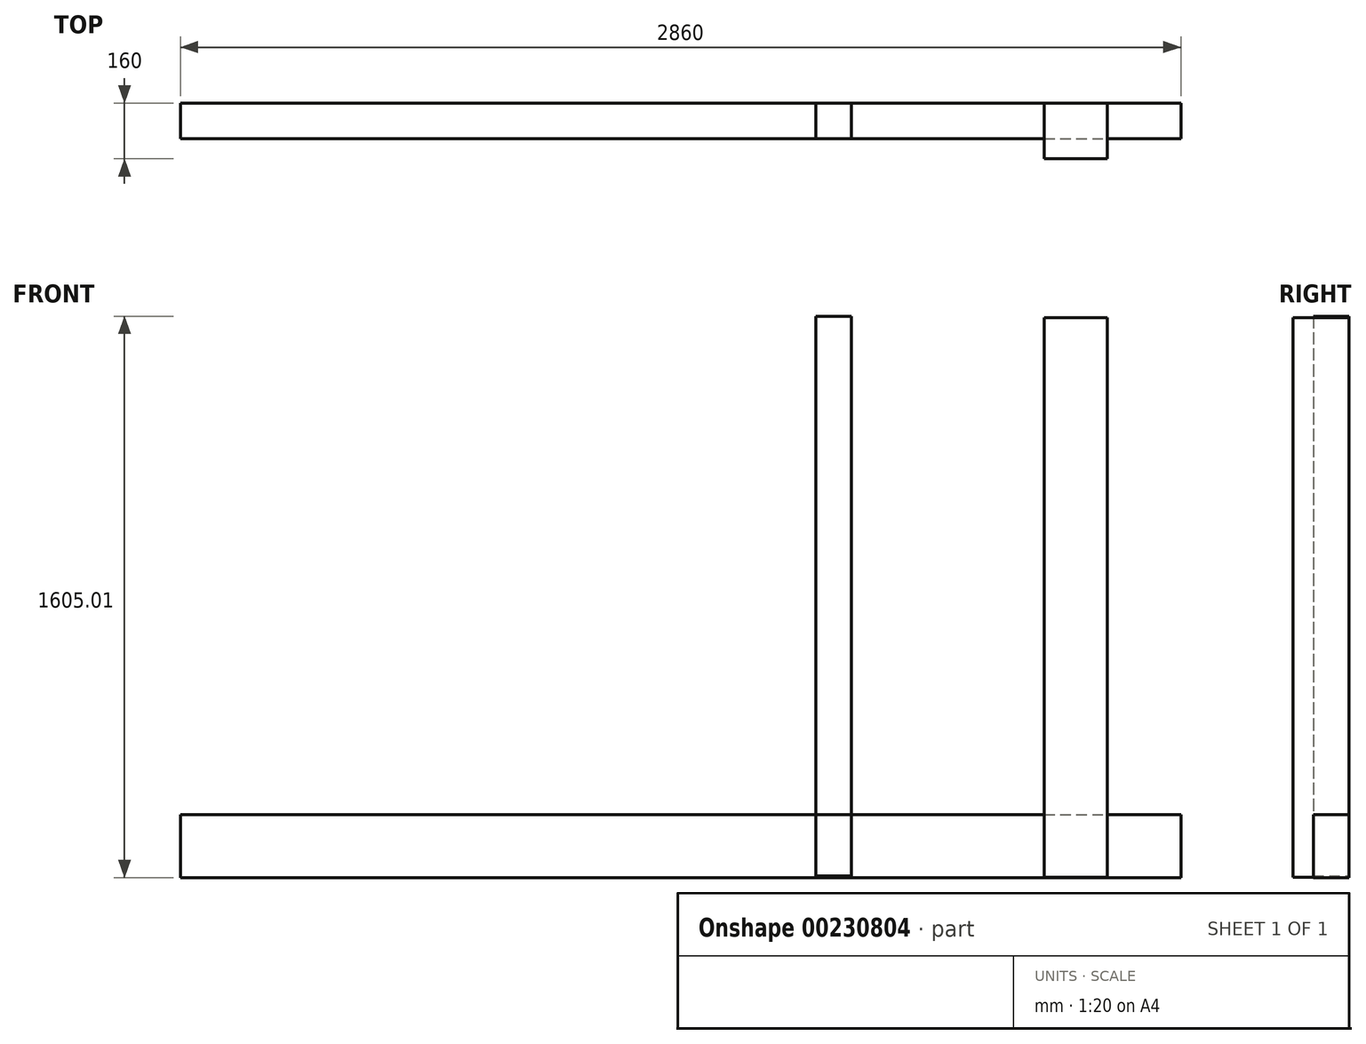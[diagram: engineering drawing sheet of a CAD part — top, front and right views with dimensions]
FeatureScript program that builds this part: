
annotation { "Feature Type Name" : "Feature", "Feature Type Description" : "" }
export const myFeature = defineFeature(function(context is Context, id is Id, definition is map)
    precondition{}
    {
        {
            var Q0;
            Q0=qCreatedBy(makeId("Front.planeOp"),FACE);
            var sketch = newSketch(context, id + "F0", { "sketchPlane" : qUnion([Q0])});
            skLineSegment(sketch, "E0.bottom", {"start": v(-353.4, 789.19) * mm, "end": v(-251.8, 789.19) * mm});
            skLineSegment(sketch, "E0.top", {"start": v(-353.4, -810.81) * mm, "end": v(-251.8, -810.81) * mm});
            skLineSegment(sketch, "E0.left", {"start": v(-353.4, 789.19) * mm, "end": v(-353.4, -810.81) * mm});
            skLineSegment(sketch, "E0.right", {"start": v(-251.8, 789.19) * mm, "end": v(-251.8, -810.81) * mm});
            skSolve(sketch);
        }
        {
            var Q0;
            Q0=makeQuery(id+"F0.imprint","IMPRINT",FACE,{"disambiguationData":[TD([[makeQuery(id+"F0.imprint","IMPRINT",EDGE,{"derivedFrom":sQuery(id+"F0.wireOp",EDGE,"E0.bottom")}),-1.0]])]});
            extrude(context, id + "F1", {"entities" : qUnion([Q0]), "depth" : 101.6 * mm});
        }
        {
            var Q0;
            Q0=qCreatedBy(makeId("Front.planeOp"),FACE);
            var sketch = newSketch(context, id + "F2", { "sketchPlane" : qUnion([Q0])});
            skLineSegment(sketch, "E1.bottom", {"start": v(299.94, 784.65) * mm, "end": v(479.94, 784.65) * mm});
            skLineSegment(sketch, "E1.top", {"start": v(299.94, -815.35) * mm, "end": v(479.94, -815.35) * mm});
            skLineSegment(sketch, "E1.left", {"start": v(299.94, 784.65) * mm, "end": v(299.94, -815.35) * mm});
            skLineSegment(sketch, "E1.right", {"start": v(479.94, 784.65) * mm, "end": v(479.94, -815.35) * mm});
            skSolve(sketch);
        }
        {
            var Q0;
            Q0=makeQuery(id+"F2.imprint","IMPRINT",FACE,{"disambiguationData":[TD([[makeQuery(id+"F2.imprint","IMPRINT",EDGE,{"derivedFrom":sQuery(id+"F2.wireOp",EDGE,"E1.bottom")}),-1.0]])]});
            extrude(context, id + "F3", {"entities" : qUnion([Q0]), "depth" : 160 * mm});
        }
        {
            var Q0;
            Q0=qCreatedBy(makeId("Front.planeOp"),FACE);
            var sketch = newSketch(context, id + "F4", { "sketchPlane" : qUnion([Q0])});
            skLineSegment(sketch, "E2.bottom", {"start": v(-2169.22, -635.82) * mm, "end": v(690.78, -635.82) * mm});
            skLineSegment(sketch, "E2.top", {"start": v(-2169.22, -815.82) * mm, "end": v(690.78, -815.82) * mm});
            skLineSegment(sketch, "E2.left", {"start": v(-2169.22, -635.82) * mm, "end": v(-2169.22, -815.82) * mm});
            skLineSegment(sketch, "E2.right", {"start": v(690.78, -635.82) * mm, "end": v(690.78, -815.82) * mm});
            skSolve(sketch);
        }
        {
            var Q0;
            Q0=makeQuery(id+"F4.imprint","IMPRINT",FACE,{"disambiguationData":[TD([[makeQuery(id+"F4.imprint","IMPRINT",EDGE,{"derivedFrom":sQuery(id+"F4.wireOp",EDGE,"E2.bottom")}),-1.0]])]});
            extrude(context, id + "F5", {"entities" : qUnion([Q0]), "depth" : 101.6 * mm});
        }
    });
